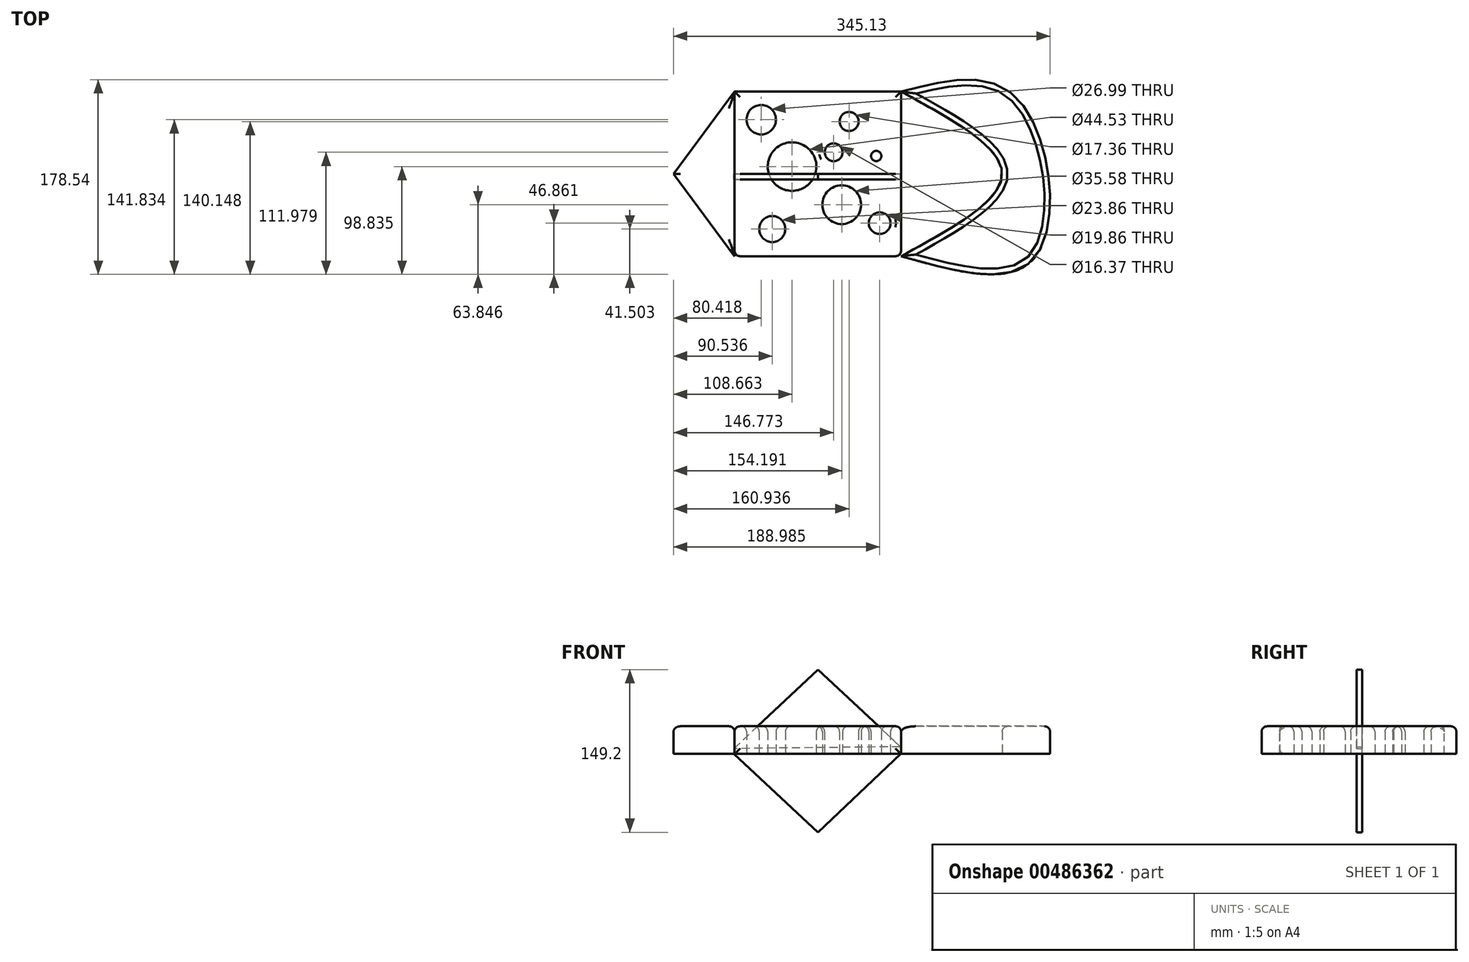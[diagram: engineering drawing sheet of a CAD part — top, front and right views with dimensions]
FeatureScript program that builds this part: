
annotation { "Feature Type Name" : "Feature", "Feature Type Description" : "" }
export const myFeature = defineFeature(function(context is Context, id is Id, definition is map)
    precondition{}
    {
        {
            var Q0;
            Q0=qCreatedBy(makeId("Top.planeOp"),FACE);
            var sketch = newSketch(context, id + "F0", { "sketchPlane" : qUnion([Q0])});
            skLineSegment(sketch, "E0.bottom", {"start": v(-76.3, 75.46) * mm, "end": v(76.3, 75.46) * mm});
            skLineSegment(sketch, "E0.top", {"start": v(-76.3, -75.46) * mm, "end": v(76.3, -75.46) * mm});
            skLineSegment(sketch, "E0.left", {"start": v(-76.3, 75.46) * mm, "end": v(-76.3, -75.46) * mm});
            skLineSegment(sketch, "E0.right", {"start": v(76.3, 75.46) * mm, "end": v(76.3, -75.46) * mm});
            skPoint(sketch, "E0.middle", {"position": v(0, 0) * mm});
            skCircle(sketch, "E1", {"center": v(-51.85, 49.74) * mm, "radius": 13.5 * mm});
            skCircle(sketch, "E2", {"center": v(-23.6, 6.74) * mm, "radius": 22.26 * mm});
            skCircle(sketch, "E3", {"center": v(28.67, 48.06) * mm, "radius": 8.68 * mm});
            skCircle(sketch, "E4", {"center": v(21.92, -28.24) * mm, "radius": 17.8 * mm});
            skCircle(sketch, "E5", {"center": v(-41.73, -50.59) * mm, "radius": 11.93 * mm});
            skCircle(sketch, "E6", {"center": v(53.54, 16.44) * mm, "radius": 4.71 * mm});
            skCircle(sketch, "E7", {"center": v(56.72, -45.23) * mm, "radius": 9.93 * mm});
            skCircle(sketch, "E8", {"center": v(14.5, 19.89) * mm, "radius": 8.19 * mm});
            skSolve(sketch);
        }
        {
            var Q0;
            Q0 = qSketchRegion(id + "F0", true);
            var Q1;
            Q1=makeQuery(id+"F0.imprint","IMPRINT",FACE,{"disambiguationData":[TD([[makeQuery(id+"F0.imprint","IMPRINT",EDGE,{"derivedFrom":sQuery(id+"F0.wireOp",EDGE,"E0.bottom")}),-1.0]])]});
            extrude(context, id + "F1", {"entities" : qUnion([Q0, Q1]), "depth" : 25.4 * mm});
        }
        {
            var Q0;
            Q0=makeQuery(id+"F1.opExtrude","CAP_FACE",FACE,{"disambiguationData":[OSD([sQuery(id+"F0.wireOp",EDGE,"E0.bottom"),sQuery(id+"F0.wireOp",EDGE,"E0.top"),sQuery(id+"F0.wireOp",EDGE,"E0.left"),sQuery(id+"F0.wireOp",EDGE,"E0.right"),sQuery(id+"F0.wireOp",EDGE,"E1"),sQuery(id+"F0.wireOp",EDGE,"E2"),sQuery(id+"F0.wireOp",EDGE,"E3"),sQuery(id+"F0.wireOp",EDGE,"E4"),sQuery(id+"F0.wireOp",EDGE,"E5"),sQuery(id+"F0.wireOp",EDGE,"E6"),sQuery(id+"F0.wireOp",EDGE,"E7"),sQuery(id+"F0.wireOp",EDGE,"E8")])],"isStart":false});
            var sketch = newSketch(context, id + "F2", { "sketchPlane" : qUnion([Q0])});
            skLineSegment(sketch, "E9", {"start": v(-76.3, 75.46) * mm, "end": v(-132.27, 0) * mm});
            skLineSegment(sketch, "E10", {"start": v(-132.27, 0) * mm, "end": v(-76.3, -75.46) * mm});
            skFitSpline(sketch, "E11", {"points": [v(76.3, 75.46) * mm, v(182.59, 69.47) * mm, v(199.96, -75.46) * mm, v(76.3, -75.46) * mm], "startDerivative": vector(391.75, 101.27) * mm, "endDerivative": vector(-460.57, 130.23) * mm});
            skFitSpline(sketch, "E12", {"points": [v(76.3, 75.46) * mm, v(169, 0) * mm, v(76.3, -75.46) * mm], "startDerivative": vector(278.07, -150.92) * mm, "endDerivative": vector(-278.07, -150.92) * mm});
            skLineSegment(sketch, "E13", {"start": v(-76.3, 75.46) * mm, "end": v(-76.3, -75.46) * mm});
            skSolve(sketch);
        }
        {
            var Q0;
            Q0 = qSketchRegion(id + "F2", true);
            extrude(context, id + "F3", {"entities" : qUnion([Q0]), "oppositeDirection" : true, "depth" : 25.4 * mm});
        }
        {
            var Q0;
            Q0=qCreatedBy(makeId("Front.planeOp"),FACE);
            var sketch = newSketch(context, id + "F4", { "sketchPlane" : qUnion([Q0])});
            skLineSegment(sketch, "E14", {"start": v(-76.85, 4.98) * mm, "end": v(0, 77.4) * mm});
            skLineSegment(sketch, "E15", {"start": v(0, 77.4) * mm, "end": v(75.74, 6.63) * mm});
            skLineSegment(sketch, "E16", {"start": v(75.74, 6.63) * mm, "end": v(-76.85, 4.98) * mm});
            skLineSegment(sketch, "E17", {"start": v(-76.85, 0) * mm, "end": v(0, -71.8) * mm});
            skLineSegment(sketch, "E18", {"start": v(0, -71.8) * mm, "end": v(76.19, 0) * mm});
            skLineSegment(sketch, "E19", {"start": v(76.19, 0) * mm, "end": v(-76.85, 0) * mm});
            skSolve(sketch);
        }
        {
            var Q0;
            Q0=makeQuery(id+"F4.imprint","IMPRINT",FACE,{"disambiguationData":[TD([[makeQuery(id+"F4.imprint","IMPRINT",EDGE,{"derivedFrom":sQuery(id+"F4.wireOp",EDGE,"E14")}),-1.0]])]});
            var Q1;
            Q1=makeQuery(id+"F4.imprint","IMPRINT",FACE,{"disambiguationData":[TD([[makeQuery(id+"F4.imprint","IMPRINT",EDGE,{"derivedFrom":sQuery(id+"F4.wireOp",EDGE,"E17")}),1.0]])]});
            extrude(context, id + "F5", {"entities" : qUnion([Q0, Q1]), "depth" : 5.08 * mm});
        }
        {
            var Q0;
            Q0=makeQuery(id+"F1.opExtrude","SWEPT_FACE",FACE,{"disambiguationData":[OSD([sQuery(id+"F0.wireOp",EDGE,"E0.top")])]});
            var Q1;
            Q1=makeQuery(id+"F1.opExtrude","CAP_FACE",FACE,{"disambiguationData":[OSD([sQuery(id+"F0.wireOp",EDGE,"E0.bottom"),sQuery(id+"F0.wireOp",EDGE,"E0.top"),sQuery(id+"F0.wireOp",EDGE,"E0.left"),sQuery(id+"F0.wireOp",EDGE,"E0.right"),sQuery(id+"F0.wireOp",EDGE,"E1"),sQuery(id+"F0.wireOp",EDGE,"E2"),sQuery(id+"F0.wireOp",EDGE,"E3"),sQuery(id+"F0.wireOp",EDGE,"E4"),sQuery(id+"F0.wireOp",EDGE,"E5"),sQuery(id+"F0.wireOp",EDGE,"E6"),sQuery(id+"F0.wireOp",EDGE,"E7"),sQuery(id+"F0.wireOp",EDGE,"E8")])],"isStart":false});
            fillet(context, id + "F6", {"entities" : qUnion([Q0, Q1]), "radius" : 5.08 * mm, "tangentPropagation" : true, "allowEdgeOverflow" : false});
        }
        {
            var Q0;
            Q0=makeQuery(id+"F3.opExtrude","CAP_FACE",FACE,{"disambiguationData":[OSD([sQuery(id+"F2.wireOp",EDGE,"E11"),sQuery(id+"F2.wireOp",EDGE,"E12")])],"isStart":true});
            fillet(context, id + "F7", {"entities" : qUnion([Q0]), "radius" : 5.08 * mm, "tangentPropagation" : true, "allowEdgeOverflow" : false});
        }
        {
            var Q0;
            Q0=makeQuery(id+"F3.opExtrude","CAP_FACE",FACE,{"disambiguationData":[OSD([sQuery(id+"F2.wireOp",EDGE,"E9"),sQuery(id+"F2.wireOp",EDGE,"E10"),sQuery(id+"F2.wireOp",EDGE,"E13")])],"isStart":true});
            fillet(context, id + "F8", {"entities" : qUnion([Q0]), "radius" : 5.08 * mm, "tangentPropagation" : true, "allowEdgeOverflow" : false});
        }
    });
